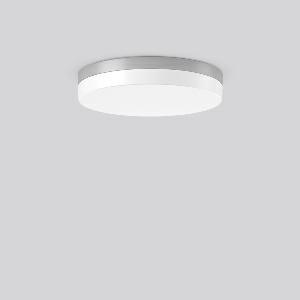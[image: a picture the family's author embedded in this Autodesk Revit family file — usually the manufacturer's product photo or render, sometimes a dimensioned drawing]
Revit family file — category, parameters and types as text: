
# Revit family: flat_slim_round_312632_004_730_4c56
name_source: partatom
category: Lighting Fixtures
units: mm (PartAtom-declared; Revit-internal decimal feet)

## family parameters
Cut with Voids When Loaded = No
Host = Face
Light Source = No
Part Type = Normal
Room Calculation Point = No
Round Connector Dimension = Use Diameter
Shared = No

## types (1)
- MultiLumen 1 830 (1 x LED Modul 830, 2400 lm, 3000)
    Apparent Load = 20 VA
    CIE Flux Codes = 39 70 90 83 100
    Color Rendering = 80
    Color Temperature = 3000
    Default Elevation = 1800 mm
    Height = 70 mm
    Lamp = 1 x LED Modul 830
    Lamp Light Flux = 2400 lm
    Lamp count = 1
    Length = 400 mm
    Lifetime = 50000 h
    Luminous efficacy = 120 lm/W
    Manufacturer = RZB
    ModVariant = No
    Model = 312632.004.730
    Mounting Place = Ceiling
    Mounting Type = Surface mounted
    Number of Poles = 1
    OnlyDefault = Yes
    Power Factor = 1
    Product Name = FLAT SLIM round
    Product group = Surface mounted ceiling and wall luminaires
    ProductGroupID = 305
    Protection Class = Protection class I
    Protection Degree = Degree of protection
    RLX_Detail_Level = 1
    RLX_Emergency_Light_Flux = 0 lm
    RLX_Emergency_Type = 0
    RLX_Emergency_Type_DB = No
    RlxData = <blob elided: 20649 chars, md5=32ec4a24>
    Socket = socket
    Standby Power = 0 W
    System Light Flux = 2400 lm
    System Power = 20 W
    Type Comments = MultiLumen 1 830
    Type Image = 312631.004.jpg
    URL = http://relux.com
    VarID = multilumen_1_830
    Voltage = 0 V
    Weight = 0.00 kg
    Width = 0 mm  [stored 0 ft]

note: [stored X ft] marks values corroborated as IEEE doubles in the binary element streams (Revit-internal decimal feet)

## geometry (parser evidence)
native form markers: Blend x4, Sweep x13
no freeform markers — native parametric forms only
